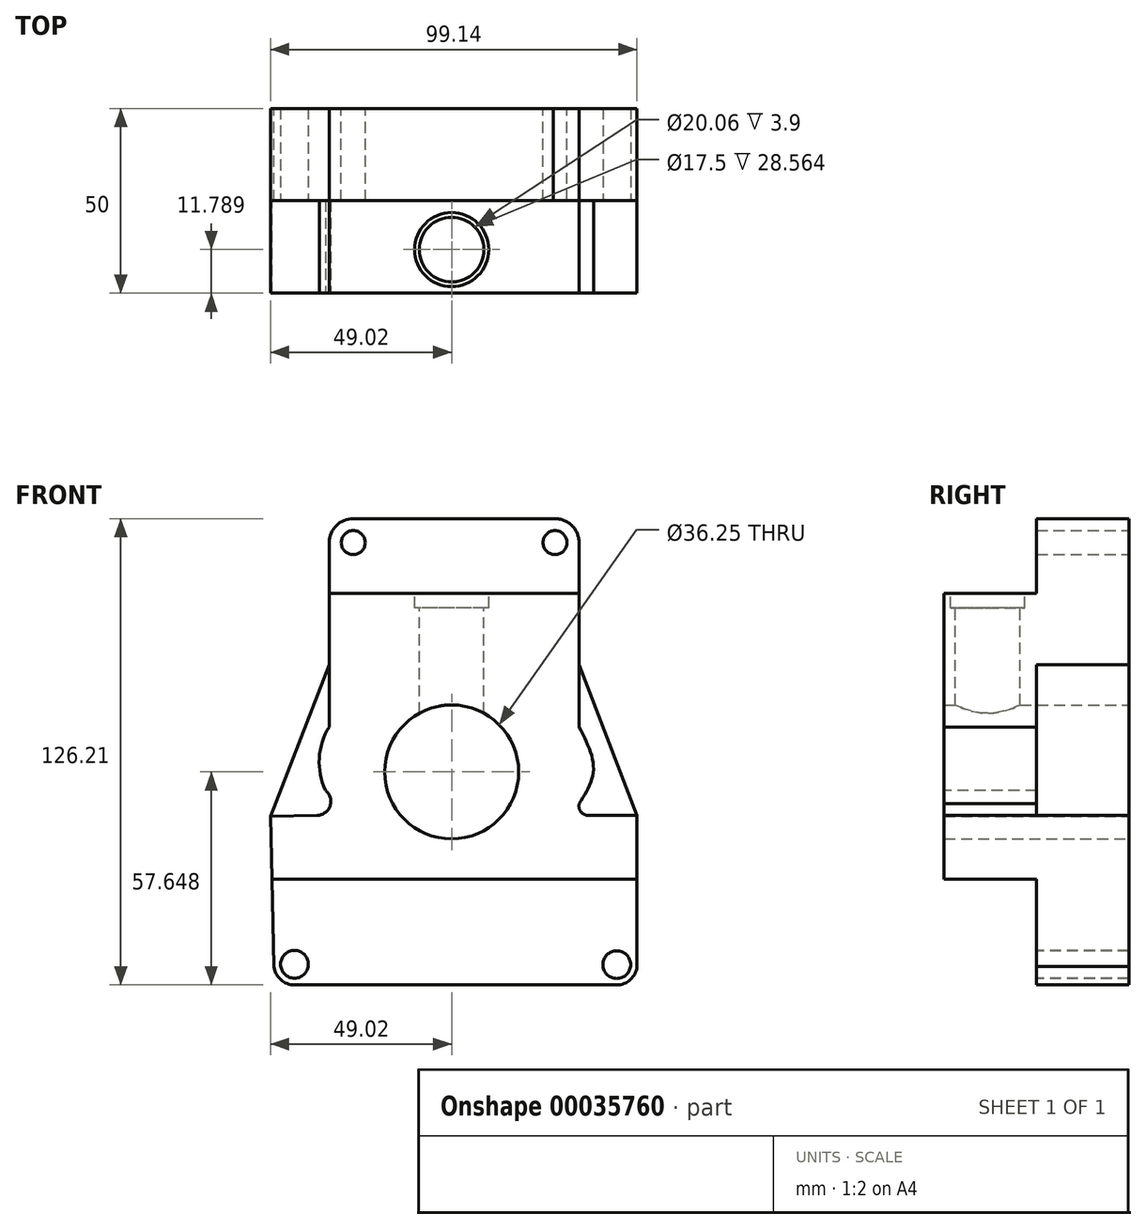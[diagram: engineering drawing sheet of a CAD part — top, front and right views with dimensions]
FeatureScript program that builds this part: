
annotation { "Feature Type Name" : "Feature", "Feature Type Description" : "" }
export const myFeature = defineFeature(function(context is Context, id is Id, definition is map)
    precondition{}
    {
        {
            var Q0;
            Q0=qCreatedBy(makeId("Front.planeOp"),FACE);
            var sketch = newSketch(context, id + "F0", { "sketchPlane" : qUnion([Q0])});
            skLineSegment(sketch, "E0", {"start": v(-33.11, 73.83) * mm, "end": v(-33.11, 55.83) * mm});
            skLineSegment(sketch, "E1", {"start": v(-26.61, 80.3) * mm, "end": v(27.54, 80.3) * mm});
            skArc(sketch, "E2", {"start": v(-26.61, 80.3) * mm, "mid": v(-31.2, 78.41) * mm, "end": v(-33.11, 73.83) * mm});
            skLineSegment(sketch, "E3", {"start": v(34.46, 73.8) * mm, "end": v(34.46, 55.83) * mm});
            skArc(sketch, "E4", {"start": v(34.46, 73.8) * mm, "mid": v(32.4, 78.55) * mm, "end": v(27.54, 80.3) * mm});
            skLineSegment(sketch, "E5", {"start": v(-33.11, 55.83) * mm, "end": v(34.46, 55.83) * mm});
            skCircle(sketch, "E6", {"center": v(-26.61, 73.8) * mm, "radius": 3.25 * mm});
            skCircle(sketch, "E7", {"center": v(27.95, 73.8) * mm, "radius": 3.25 * mm});
            skLineSegment(sketch, "E8", {"start": v(-33.11, 55.83) * mm, "end": v(-33.11, 25.75) * mm});
            skLineSegment(sketch, "E9", {"start": v(34.46, 55.83) * mm, "end": v(34.46, 25.75) * mm});
            skFitSpline(sketch, "E10", {"points": [v(-33.11, 25.75) * mm, v(-36.14, 15.68) * mm, v(-33.11, 4.63) * mm], "startDerivative": vector(-9.14, -20.33) * mm, "endDerivative": vector(9.01, -21.91) * mm});
            skFitSpline(sketch, "E11", {"points": [v(-33.11, 4.63) * mm, v(-33.11, 0) * mm, v(-36.38, 0) * mm], "startDerivative": vector(1.94, -10.83) * mm, "endDerivative": vector(-8.8, 1.94) * mm});
            skFitSpline(sketch, "E12", {"points": [v(34.46, 25.75) * mm, v(37.63, 12.66) * mm, v(34.46, 4.63) * mm], "startDerivative": vector(9.29, -25.1) * mm, "endDerivative": vector(-10, -16.85) * mm});
            skFitSpline(sketch, "E13", {"points": [v(34.46, 4.63) * mm, v(34.46, 0) * mm, v(37.63, 0) * mm], "startDerivative": vector(-1.92, -10.77) * mm, "endDerivative": vector(8.6, 1.92) * mm});
            skCircle(sketch, "E14", {"center": v(0, 12.66) * mm, "radius": 17.02 * mm});
            skLineSegment(sketch, "E15", {"start": v(-36.38, 0) * mm, "end": v(-49.02, -0.3) * mm});
            skLineSegment(sketch, "E16", {"start": v(37.63, 0) * mm, "end": v(50.12, 0) * mm});
            skLineSegment(sketch, "E17", {"start": v(-49.02, -0.3) * mm, "end": v(-48.07, -40.94) * mm});
            skLineSegment(sketch, "E18", {"start": v(50.12, 0) * mm, "end": v(50.12, -40.94) * mm});
            skLineSegment(sketch, "E19", {"start": v(-42.52, -45.89) * mm, "end": v(44.66, -45.89) * mm});
            skArc(sketch, "E20", {"start": v(44.66, -45.89) * mm, "mid": v(48.34, -44.47) * mm, "end": v(50.12, -40.94) * mm});
            skArc(sketch, "E21", {"start": v(-48.07, -40.94) * mm, "mid": v(-46.23, -44.47) * mm, "end": v(-42.52, -45.89) * mm});
            skLineSegment(sketch, "E22", {"start": v(-33.11, 40.8) * mm, "end": v(-49.02, -0.3) * mm});
            skLineSegment(sketch, "E23", {"start": v(34.46, 40.8) * mm, "end": v(50.12, 0) * mm});
            skCircle(sketch, "E24", {"center": v(-42.52, -40.3) * mm, "radius": 3.25 * mm});
            skCircle(sketch, "E25", {"center": v(44.66, -40.4) * mm, "radius": 3.25 * mm});
            skLineSegment(sketch, "E26", {"start": v(-48.66, -15.7) * mm, "end": v(50.12, -15.7) * mm});
            skSolve(sketch);
        }
        {
            var Q0;
            Q0=makeQuery(id+"F0.imprint","IMPRINT",FACE,{"disambiguationData":[TD([[makeQuery(id+"F0.imprint","IMPRINT",EDGE,{"derivedFrom":sQuery(id+"F0.wireOp",EDGE,"E6")}),1.0]])]});
            var Q1;
            Q1=makeQuery(id+"F0.imprint","IMPRINT",FACE,{"disambiguationData":[TD([[makeQuery(id+"F0.imprint","IMPRINT",EDGE,{"derivedFrom":sQuery(id+"F0.wireOp",EDGE,"E7")}),1.0]])]});
            var Q2;
            {var subQ0=sQuery(id+"F0.wireOp",EDGE,"E10");Q2=makeQuery(id+"F0.imprint","IMPRINT",FACE,{"disambiguationData":[TD([[makeQuery(id+"F0.imprint","IMPRINT",EDGE,{"derivedFrom":subQ0}),-1.0]])]});}
            var Q3;
            {var subQ0=sQuery(id+"F0.wireOp",EDGE,"E12");Q3=makeQuery(id+"F0.imprint","IMPRINT",FACE,{"disambiguationData":[TD([[makeQuery(id+"F0.imprint","IMPRINT",EDGE,{"derivedFrom":subQ0}),1.0]])]});}
            var Q4;
            Q4=makeQuery(id+"F0.imprint","IMPRINT",FACE,{"disambiguationData":[TD([[makeQuery(id+"F0.imprint","IMPRINT",EDGE,{"derivedFrom":sQuery(id+"F0.wireOp",EDGE,"E14")}),1.0]])]});
            var Q5;
            Q5=makeQuery(id+"F0.imprint","IMPRINT",FACE,{"disambiguationData":[TD([[makeQuery(id+"F0.imprint","IMPRINT",EDGE,{"derivedFrom":sQuery(id+"F0.wireOp",EDGE,"E24")}),1.0]])]});
            var Q6;
            Q6=makeQuery(id+"F0.imprint","IMPRINT",FACE,{"disambiguationData":[TD([[makeQuery(id+"F0.imprint","IMPRINT",EDGE,{"derivedFrom":sQuery(id+"F0.wireOp",EDGE,"E25")}),1.0]])]});
            var Q7;
            Q7=makeQuery(id+"F0.imprint","IMPRINT",FACE,{"disambiguationData":[TD([[makeQuery(id+"F0.imprint","IMPRINT",EDGE,{"derivedFrom":sQuery(id+"F0.wireOp",EDGE,"E0")}),1.0]])]});
            var Q8;
            Q8=makeQuery(id+"F0.imprint","IMPRINT",FACE,{"disambiguationData":[TD([[makeQuery(id+"F0.imprint","IMPRINT",EDGE,{"derivedFrom":sQuery(id+"F0.wireOp",EDGE,"E19")}),1.0]])]});
            var Q9;
            {var subQ1=sQuery(id+"F0.wireOp",EDGE,"E5");Q9=makeQuery(id+"F0.imprint","IMPRINT",FACE,{"disambiguationData":[TD([[makeQuery(id+"F0.imprint","IMPRINT",EDGE,{"derivedFrom":subQ1}),-1.0]])]});}
            extrude(context, id + "F1", {"entities" : qUnion([Q0, Q1, Q2, Q3, Q4, Q5, Q6, Q7, Q8, Q9]), "depth" : 25 * mm});
        }
        {
            var Q0;
            Q0=makeQuery(id+"F1.opExtrude","CAP_FACE",FACE,{"disambiguationData":[OSD([sQuery(id+"F0.wireOp",EDGE,"E0"),sQuery(id+"F0.wireOp",EDGE,"E1"),sQuery(id+"F0.wireOp",EDGE,"E2"),sQuery(id+"F0.wireOp",EDGE,"E3"),sQuery(id+"F0.wireOp",EDGE,"E4"),sQuery(id+"F0.wireOp",EDGE,"E8"),sQuery(id+"F0.wireOp",EDGE,"E9"),sQuery(id+"F0.wireOp",EDGE,"E17"),sQuery(id+"F0.wireOp",EDGE,"E18"),sQuery(id+"F0.wireOp",EDGE,"E19"),sQuery(id+"F0.wireOp",EDGE,"E20"),sQuery(id+"F0.wireOp",EDGE,"E21"),sQuery(id+"F0.wireOp",EDGE,"E22"),sQuery(id+"F0.wireOp",EDGE,"E23")])],"isStart":true});
            var sketch = newSketch(context, id + "F2", { "sketchPlane" : qUnion([Q0])});
            skCircle(sketch, "E27", {"center": v(-27.95, 73.8) * mm, "radius": 3.25 * mm});
            skCircle(sketch, "E28", {"center": v(26.61, 73.8) * mm, "radius": 3.25 * mm});
            skCircle(sketch, "E29", {"center": v(42.52, -40.3) * mm, "radius": 3.45 * mm});
            skCircle(sketch, "E30", {"center": v(-44.66, -40.4) * mm, "radius": 3.37 * mm});
            skSolve(sketch);
        }
        {
            var Q0;
            Q0=makeQuery(id+"F2.imprint","IMPRINT",FACE,{"disambiguationData":[TD([[makeQuery(id+"F2.imprint","IMPRINT",EDGE,{"derivedFrom":sQuery(id+"F2.wireOp",EDGE,"E27")}),1.0]])]});
            extrude(context, id + "F3", {"entities" : qUnion([Q0]), "operationType" : NewBodyOperationType.REMOVE, "oppositeDirection" : true, "depth" : 70 * mm});
        }
        {
            var Q0;
            Q0=makeQuery(id+"F2.imprint","IMPRINT",FACE,{"disambiguationData":[TD([[makeQuery(id+"F2.imprint","IMPRINT",EDGE,{"derivedFrom":sQuery(id+"F2.wireOp",EDGE,"E28")}),1.0]])]});
            extrude(context, id + "F4", {"entities" : qUnion([Q0]), "operationType" : NewBodyOperationType.REMOVE, "oppositeDirection" : true, "depth" : 70 * mm});
        }
        {
            var Q0;
            Q0=makeQuery(id+"F1.opExtrude","CAP_FACE",FACE,{"disambiguationData":[OSD([sQuery(id+"F0.wireOp",EDGE,"E0"),sQuery(id+"F0.wireOp",EDGE,"E1"),sQuery(id+"F0.wireOp",EDGE,"E2"),sQuery(id+"F0.wireOp",EDGE,"E3"),sQuery(id+"F0.wireOp",EDGE,"E4"),sQuery(id+"F0.wireOp",EDGE,"E8"),sQuery(id+"F0.wireOp",EDGE,"E9"),sQuery(id+"F0.wireOp",EDGE,"E17"),sQuery(id+"F0.wireOp",EDGE,"E18"),sQuery(id+"F0.wireOp",EDGE,"E19"),sQuery(id+"F0.wireOp",EDGE,"E20"),sQuery(id+"F0.wireOp",EDGE,"E21"),sQuery(id+"F0.wireOp",EDGE,"E22"),sQuery(id+"F0.wireOp",EDGE,"E23")])],"isStart":false});
            var sketch = newSketch(context, id + "F5", { "sketchPlane" : qUnion([Q0])});
            skLineSegment(sketch, "E31", {"start": v(34.46, 40.8) * mm, "end": v(34.46, 20.6) * mm});
            skLineSegment(sketch, "E32", {"start": v(-33.11, 40.8) * mm, "end": v(-33.11, 20.6) * mm});
            skLineSegment(sketch, "E33", {"start": v(-49.02, -0.3) * mm, "end": v(-36.38, 0) * mm});
            skArc(sketch, "E34", {"start": v(-33.11, 20.6) * mm, "mid": v(-37.16, 12.97) * mm, "end": v(-34.8, 4.67) * mm});
            skPoint(sketch, "E35", {"position": v(-34.8, 4.67) * mm});
            skArc(sketch, "E36", {"start": v(-36.38, 0) * mm, "mid": v(-33.95, 1.78) * mm, "end": v(-34.8, 4.67) * mm});
            skLineSegment(sketch, "E37", {"start": v(50.12, 0) * mm, "end": v(37.38, 0) * mm});
            skArc(sketch, "E38", {"start": v(36.06, 5.27) * mm, "mid": v(37.57, 13.18) * mm, "end": v(34.46, 20.6) * mm});
            skPoint(sketch, "E39", {"position": v(36.06, 5.27) * mm});
            skArc(sketch, "E40", {"start": v(36.06, 5.27) * mm, "mid": v(34.66, 2.12) * mm, "end": v(37.38, 0) * mm});
            skLineSegment(sketch, "E41", {"start": v(-48.63, -17.2) * mm, "end": v(50.12, -17.2) * mm});
            skPoint(sketch, "E41.endSnap0", {"position": v(50.12, -20.47) * mm});
            skCircle(sketch, "E42", {"center": v(0, 11.76) * mm, "radius": 18.13 * mm});
            skLineSegment(sketch, "E43", {"start": v(-33.11, 40.8) * mm, "end": v(34.46, 40.8) * mm});
            skLineSegment(sketch, "E44", {"start": v(-33.11, 60.1) * mm, "end": v(34.46, 60.1) * mm});
            skSolve(sketch);
        }
        {
            var Q0;
            Q0=makeQuery(id+"F5.imprint","IMPRINT",FACE,{"disambiguationData":[TD([[makeQuery(id+"F5.imprint","IMPRINT",EDGE,{"derivedFrom":sQuery(id+"F5.wireOp",EDGE,"E31")}),-1.0]])]});
            var Q1;
            Q1=makeQuery(id+"F5.imprint","IMPRINT",FACE,{"disambiguationData":[TD([[makeQuery(id+"F5.imprint","IMPRINT",EDGE,{"derivedFrom":sQuery(id+"F5.wireOp",EDGE,"E32")}),-1.0]])]});
            var Q2;
            Q2=makeQuery(id+"F5.imprint","IMPRINT",FACE,{"disambiguationData":[TD([[makeQuery(id+"F5.imprint","IMPRINT",EDGE,{"derivedFrom":sQuery(id+"F5.wireOp",EDGE,"E31")}),1.0]])]});
            extrude(context, id + "F6", {"entities" : qUnion([Q0, Q1, Q2]), "operationType" : NewBodyOperationType.ADD, "depth" : 25 * mm});
        }
        {
            var Q0;
            Q0=makeQuery(id+"F6.boolean.opBoolean","SPLIT",FACE,{"disambiguationData":[TD([makeQuery(id+"F6.opExtrude","SWEPT_FACE",FACE,{"disambiguationData":[OSD([sQuery(id+"F5.wireOp",EDGE,"E42")])]})])],"derivedFrom":makeQuery(id+"F1.opExtrude","CAP_FACE",FACE,{"disambiguationData":[OSD([sQuery(id+"F0.wireOp",EDGE,"E0"),sQuery(id+"F0.wireOp",EDGE,"E1"),sQuery(id+"F0.wireOp",EDGE,"E2"),sQuery(id+"F0.wireOp",EDGE,"E3"),sQuery(id+"F0.wireOp",EDGE,"E4"),sQuery(id+"F0.wireOp",EDGE,"E8"),sQuery(id+"F0.wireOp",EDGE,"E9"),sQuery(id+"F0.wireOp",EDGE,"E17"),sQuery(id+"F0.wireOp",EDGE,"E18"),sQuery(id+"F0.wireOp",EDGE,"E19"),sQuery(id+"F0.wireOp",EDGE,"E20"),sQuery(id+"F0.wireOp",EDGE,"E21"),sQuery(id+"F0.wireOp",EDGE,"E22"),sQuery(id+"F0.wireOp",EDGE,"E23")])],"isStart":false})});
            extrude(context, id + "F7", {"entities" : qUnion([Q0]), "operationType" : NewBodyOperationType.REMOVE, "oppositeDirection" : true, "depth" : 70 * mm});
        }
        {
            var Q0;
            Q0=makeQuery(id+"F6.opExtrude","CAP_FACE",FACE,{"disambiguationData":[OSD([sQuery(id+"F0.wireOp",EDGE,"E17"),sQuery(id+"F0.wireOp",EDGE,"E18"),sQuery(id+"F0.wireOp",EDGE,"E22"),sQuery(id+"F0.wireOp",EDGE,"E23"),sQuery(id+"F5.wireOp",EDGE,"E41"),sQuery(id+"F5.wireOp",EDGE,"E42"),sQuery(id+"F5.wireOp",EDGE,"E43")])],"isStart":false});
            var sketch = newSketch(context, id + "F8", { "sketchPlane" : qUnion([Q0])});
            skLineSegment(sketch, "E45", {"start": v(-33.11, 40.8) * mm, "end": v(-33.11, 23.93) * mm});
            skLineSegment(sketch, "E46", {"start": v(34.46, 23.93) * mm, "end": v(34.46, 40.8) * mm});
            skLineSegment(sketch, "E47", {"start": v(-49.02, -0.3) * mm, "end": v(-36.38, 0) * mm});
            skArc(sketch, "E48", {"start": v(-36.38, 0) * mm, "mid": v(-32.87, 2.6) * mm, "end": v(-34.12, 6.78) * mm});
            skArc(sketch, "E49", {"start": v(-33.11, 23.93) * mm, "mid": v(-35.8, 15.48) * mm, "end": v(-34.12, 6.78) * mm});
            skFitSpline(sketch, "E50", {"points": [v(34.46, 23.93) * mm, v(38.36, 12.52) * mm, v(34.46, 3.12) * mm], "startDerivative": vector(11.55, -22.48) * mm, "endDerivative": vector(-11.88, -19.1) * mm});
            skLineSegment(sketch, "E51", {"start": v(50.12, 0) * mm, "end": v(36.99, 0) * mm});
            skArc(sketch, "E52", {"start": v(34.46, 3.12) * mm, "mid": v(34.98, 0.96) * mm, "end": v(36.99, 0) * mm});
            skSolve(sketch);
        }
        {
            var Q0;
            Q0=makeQuery(id+"F8.imprint","IMPRINT",FACE,{"disambiguationData":[TD([[makeQuery(id+"F8.imprint","IMPRINT",EDGE,{"derivedFrom":sQuery(id+"F8.wireOp",EDGE,"E45")}),-1.0]])]});
            var Q1;
            Q1=makeQuery(id+"F8.imprint","IMPRINT",FACE,{"disambiguationData":[TD([[makeQuery(id+"F8.imprint","IMPRINT",EDGE,{"derivedFrom":sQuery(id+"F8.wireOp",EDGE,"E46")}),-1.0]])]});
            extrude(context, id + "F9", {"entities" : qUnion([Q0, Q1]), "operationType" : NewBodyOperationType.REMOVE, "oppositeDirection" : true, "depth" : 25 * mm});
        }
        {
            var Q0;
            {var subQ0=sQuery(id+"F5.wireOp",EDGE,"E43");Q0=makeQuery(id+"F5.imprint","IMPRINT",FACE,{"disambiguationData":[TD([[makeQuery(id+"F5.imprint","IMPRINT",EDGE,{"derivedFrom":subQ0}),1.0]])]});}
            extrude(context, id + "F10", {"entities" : qUnion([Q0]), "operationType" : NewBodyOperationType.ADD, "depth" : 25 * mm});
        }
        {
            var Q0;
            Q0=makeQuery(id+"F10.opExtrude","SWEPT_FACE",FACE,{"disambiguationData":[OSD([sQuery(id+"F5.wireOp",EDGE,"E44")])]});
            var sketch = newSketch(context, id + "F11", { "sketchPlane" : qUnion([Q0])});
            skCircle(sketch, "E53", {"center": v(0, -38.21) * mm, "radius": 10.03 * mm});
            skSolve(sketch);
        }
        {
            var Q0;
            Q0=makeQuery(id+"F11.imprint","IMPRINT",FACE,{"disambiguationData":[TD([[makeQuery(id+"F11.imprint","IMPRINT",EDGE,{"derivedFrom":sQuery(id+"F11.wireOp",EDGE,"E53")}),1.0]])]});
            extrude(context, id + "F12", {"entities" : qUnion([Q0]), "operationType" : NewBodyOperationType.REMOVE, "oppositeDirection" : true, "depth" : 3.9 * mm});
        }
        {
            var Q0;
            Q0=makeQuery(id+"F12.boolean.opBoolean","COPY",FACE,{"derivedFrom":makeQuery(id+"F12.opExtrude","CAP_FACE",FACE,{"disambiguationData":[OSD([sQuery(id+"F11.wireOp",EDGE,"E53")])],"isStart":false})});
            var sketch = newSketch(context, id + "F13", { "sketchPlane" : qUnion([Q0])});
            skCircle(sketch, "E54", {"center": v(0, -38.21) * mm, "radius": 8.75 * mm});
            skSolve(sketch);
        }
        {
            var Q0;
            Q0=makeQuery(id+"F13.imprint","IMPRINT",FACE,{"disambiguationData":[TD([[makeQuery(id+"F13.imprint","IMPRINT",EDGE,{"derivedFrom":sQuery(id+"F13.wireOp",EDGE,"E54")}),1.0]])]});
            extrude(context, id + "F14", {"entities" : qUnion([Q0]), "operationType" : NewBodyOperationType.REMOVE, "oppositeDirection" : true, "depth" : 45.3 * mm});
        }
        {
            var Q0;
            {var subQ0=sQuery(id+"F0.wireOp",EDGE,"E20");var subQ1=sQuery(id+"F0.wireOp",EDGE,"E19");var subQ2=sQuery(id+"F0.wireOp",EDGE,"E18");var subQ3=sQuery(id+"F0.wireOp",EDGE,"E17");var subQ4=sQuery(id+"F0.wireOp",EDGE,"E21");Q0=makeQuery(id+"F6.boolean.opBoolean","SPLIT",FACE,{"disambiguationData":[TD([makeQuery(id+"F1.opExtrude","SWEPT_FACE",FACE,{"disambiguationData":[OSD([subQ3])]})])],"derivedFrom":makeQuery(id+"F1.opExtrude","CAP_FACE",FACE,{"disambiguationData":[OSD([sQuery(id+"F0.wireOp",EDGE,"E0"),sQuery(id+"F0.wireOp",EDGE,"E1"),sQuery(id+"F0.wireOp",EDGE,"E2"),sQuery(id+"F0.wireOp",EDGE,"E3"),sQuery(id+"F0.wireOp",EDGE,"E4"),sQuery(id+"F0.wireOp",EDGE,"E8"),sQuery(id+"F0.wireOp",EDGE,"E9"),subQ3,subQ2,subQ1,subQ0,subQ4,sQuery(id+"F0.wireOp",EDGE,"E22"),sQuery(id+"F0.wireOp",EDGE,"E23")])],"isStart":false})});}
            var sketch = newSketch(context, id + "F15", { "sketchPlane" : qUnion([Q0])});
            skCircle(sketch, "E55", {"center": v(-42.52, -40.3) * mm, "radius": 3.75 * mm});
            skCircle(sketch, "E56", {"center": v(44.66, -40.4) * mm, "radius": 3.75 * mm});
            skSolve(sketch);
        }
        {
            var Q0;
            Q0=makeQuery(id+"F15.imprint","IMPRINT",FACE,{"disambiguationData":[TD([[makeQuery(id+"F15.imprint","IMPRINT",EDGE,{"derivedFrom":sQuery(id+"F15.wireOp",EDGE,"E55")}),1.0]])]});
            extrude(context, id + "F16", {"entities" : qUnion([Q0]), "operationType" : NewBodyOperationType.REMOVE, "oppositeDirection" : true, "depth" : 70 * mm});
        }
        {
            var Q0;
            Q0=makeQuery(id+"F15.imprint","IMPRINT",FACE,{"disambiguationData":[TD([[makeQuery(id+"F15.imprint","IMPRINT",EDGE,{"derivedFrom":sQuery(id+"F15.wireOp",EDGE,"E56")}),1.0]])]});
            extrude(context, id + "F17", {"entities" : qUnion([Q0]), "operationType" : NewBodyOperationType.REMOVE, "oppositeDirection" : true, "depth" : 70 * mm});
        }
    });
